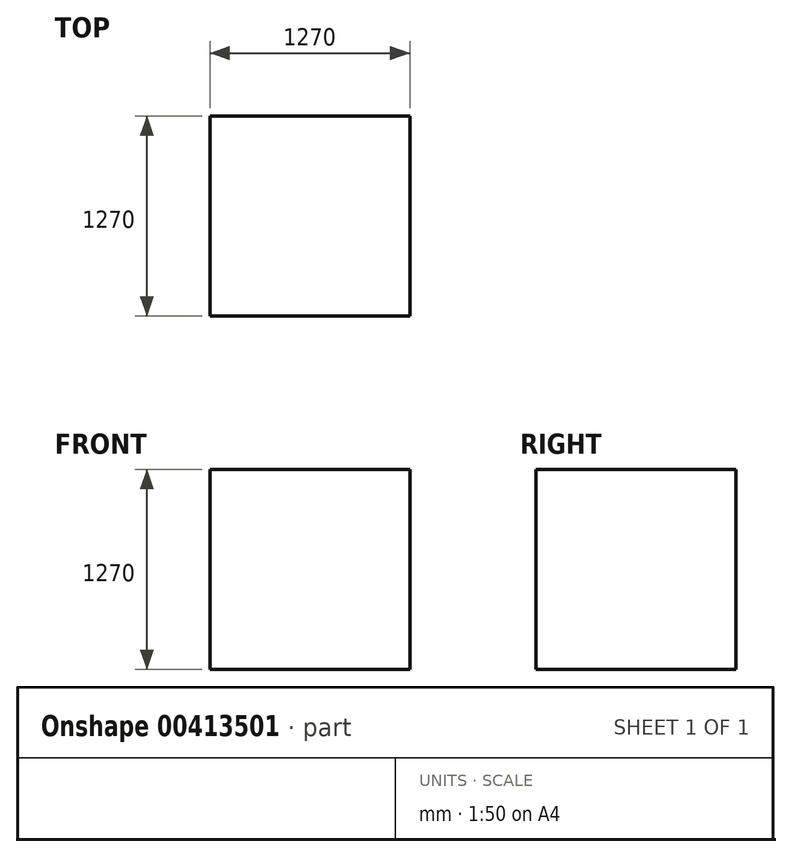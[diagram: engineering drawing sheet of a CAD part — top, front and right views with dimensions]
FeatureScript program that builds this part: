
annotation { "Feature Type Name" : "Feature", "Feature Type Description" : "" }
export const myFeature = defineFeature(function(context is Context, id is Id, definition is map)
    precondition{}
    {
        {
            var Q0;
            Q0=qCreatedBy(makeId("Front.planeOp"),FACE);
            var sketch = newSketch(context, id + "F0", { "sketchPlane" : qUnion([Q0])});
            skLineSegment(sketch, "E0.bottom", {"start": v(-635, 635) * mm, "end": v(635, 635) * mm});
            skLineSegment(sketch, "E0.top", {"start": v(-635, -635) * mm, "end": v(635, -635) * mm});
            skLineSegment(sketch, "E0.left", {"start": v(-635, 635) * mm, "end": v(-635, -635) * mm});
            skLineSegment(sketch, "E0.right", {"start": v(635, 635) * mm, "end": v(635, -635) * mm});
            skPoint(sketch, "E0.middle", {"position": v(0, 0) * mm});
            skSolve(sketch);
        }
        {
            var Q0;
            Q0=makeQuery(id+"F0.imprint","IMPRINT",FACE,{"disambiguationData":[TD([[makeQuery(id+"F0.imprint","IMPRINT",EDGE,{"derivedFrom":sQuery(id+"F0.wireOp",EDGE,"E0.bottom")}),-1.0]])]});
            extrude(context, id + "F1", {"entities" : qUnion([Q0]), "depth" : 1270 * mm});
        }
    });
